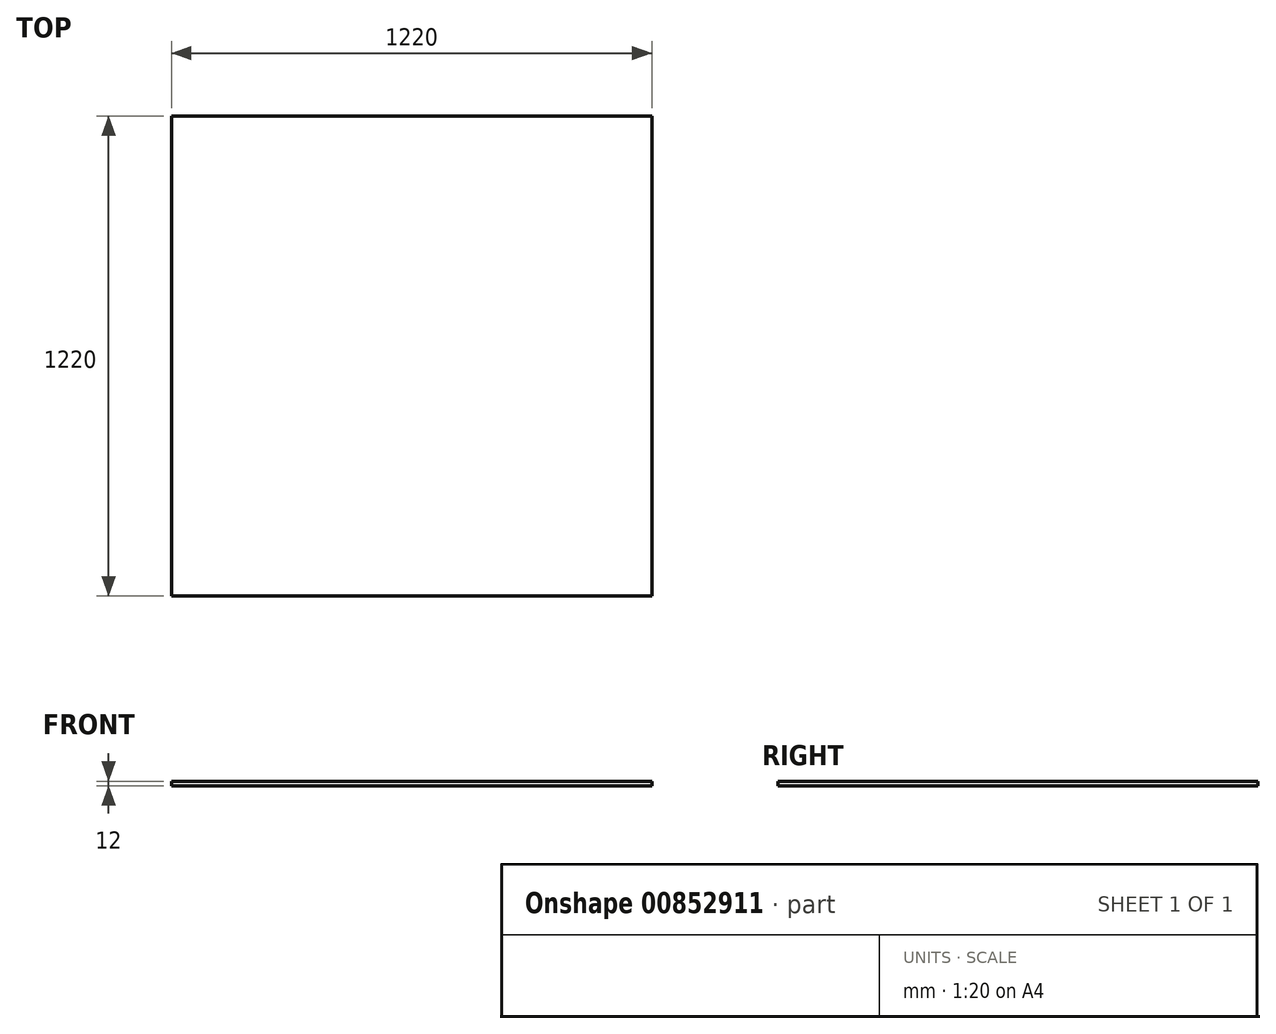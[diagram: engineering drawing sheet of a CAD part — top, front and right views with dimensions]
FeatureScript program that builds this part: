
annotation { "Feature Type Name" : "Feature", "Feature Type Description" : "" }
export const myFeature = defineFeature(function(context is Context, id is Id, definition is map)
    precondition{}
    {
        {
            var Q0;
            Q0=qCreatedBy(makeId("Top.planeOp"),FACE);
            var sketch = newSketch(context, id + "F0", { "sketchPlane" : qUnion([Q0])});
            skLineSegment(sketch, "E0.bottom", {"start": v(610, -610) * mm, "end": v(-610, -610) * mm});
            skLineSegment(sketch, "E0.top", {"start": v(610, 610) * mm, "end": v(-610, 610) * mm});
            skLineSegment(sketch, "E0.left", {"start": v(610, -610) * mm, "end": v(610, 610) * mm});
            skLineSegment(sketch, "E0.right", {"start": v(-610, -610) * mm, "end": v(-610, 610) * mm});
            skPoint(sketch, "E0.middle", {"position": v(0, 0) * mm});
            skSolve(sketch);
        }
        {
            var Q0;
            Q0=makeQuery(id+"F0.imprint","IMPRINT",FACE,{"disambiguationData":[TD([[makeQuery(id+"F0.imprint","IMPRINT",EDGE,{"derivedFrom":sQuery(id+"F0.wireOp",EDGE,"E0.bottom")}),-1.0]])]});
            extrude(context, id + "F1", {"entities" : qUnion([Q0]), "depth" : 12 * mm, "offsetDistance" : 25 * mm});
        }
    });
